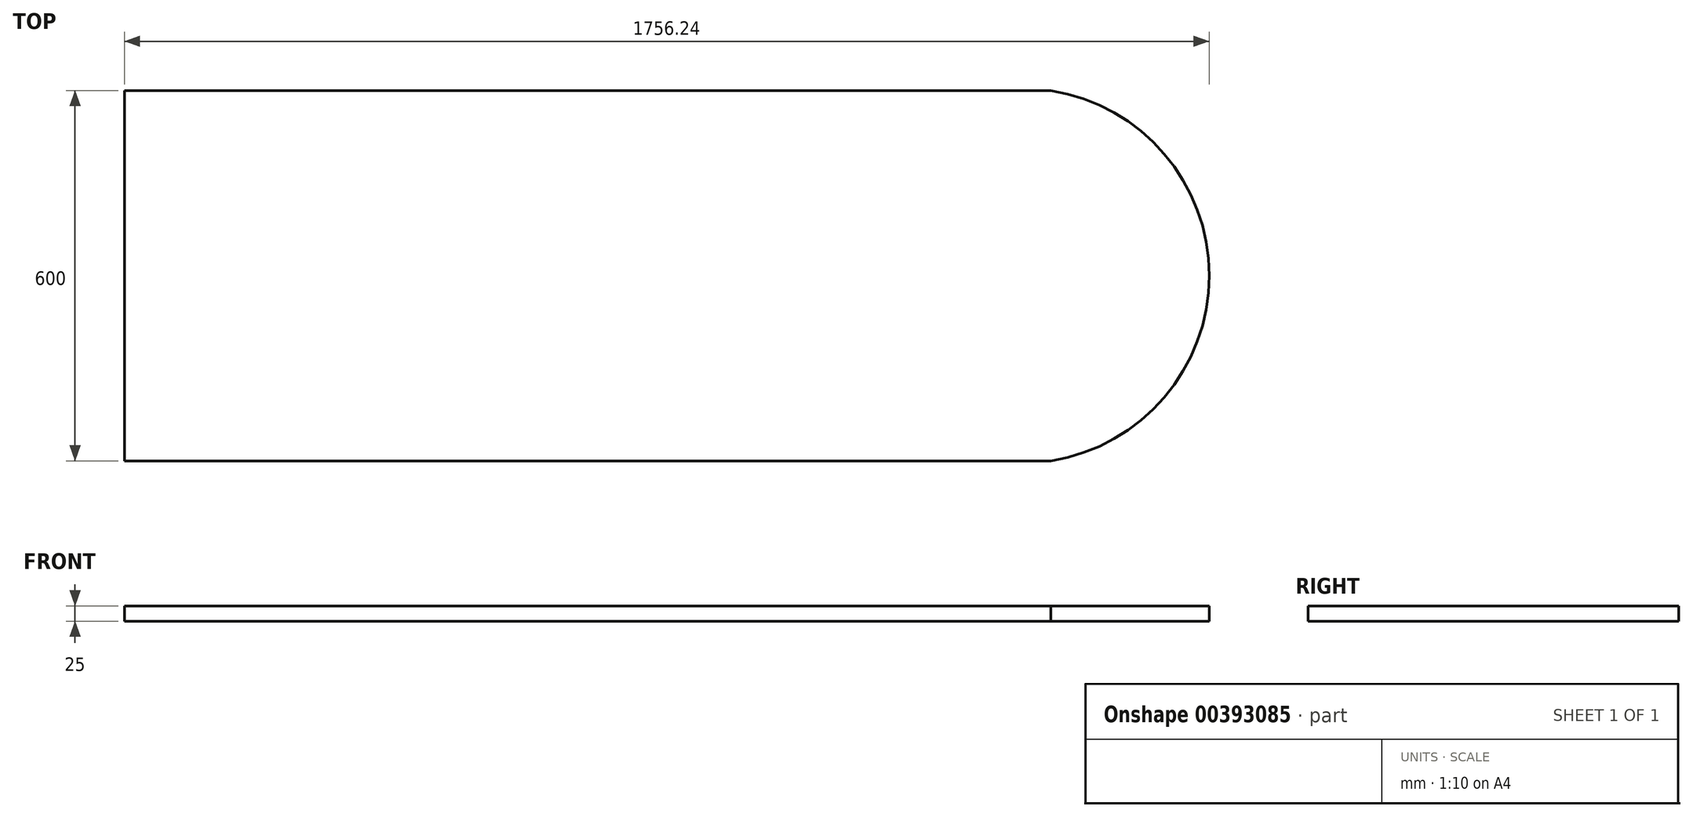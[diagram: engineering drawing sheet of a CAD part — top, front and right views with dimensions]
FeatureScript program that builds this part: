
annotation { "Feature Type Name" : "Feature", "Feature Type Description" : "" }
export const myFeature = defineFeature(function(context is Context, id is Id, definition is map)
    precondition{}
    {
        {
            var Q0;
            Q0=qCreatedBy(makeId("Top.planeOp"),FACE);
            var sketch = newSketch(context, id + "F0", { "sketchPlane" : qUnion([Q0])});
            skLineSegment(sketch, "E0.bottom", {"start": v(-750, -300) * mm, "end": v(750, -300) * mm});
            skLineSegment(sketch, "E0.top", {"start": v(-750, 300) * mm, "end": v(750, 300) * mm});
            skLineSegment(sketch, "E0.left", {"start": v(-750, -300) * mm, "end": v(-750, 300) * mm});
            skPoint(sketch, "E0.middle", {"position": v(0, 0) * mm});
            skArc(sketch, "E1", {"start": v(750, -300) * mm, "mid": v(1006.24, 0) * mm, "end": v(750, 300) * mm});
            skSolve(sketch);
        }
        {
            var Q0;
            Q0 = qSketchRegion(id + "F0", true);
            extrude(context, id + "F1", {"entities" : qUnion([Q0]), "depth" : 25 * mm});
        }
    });
